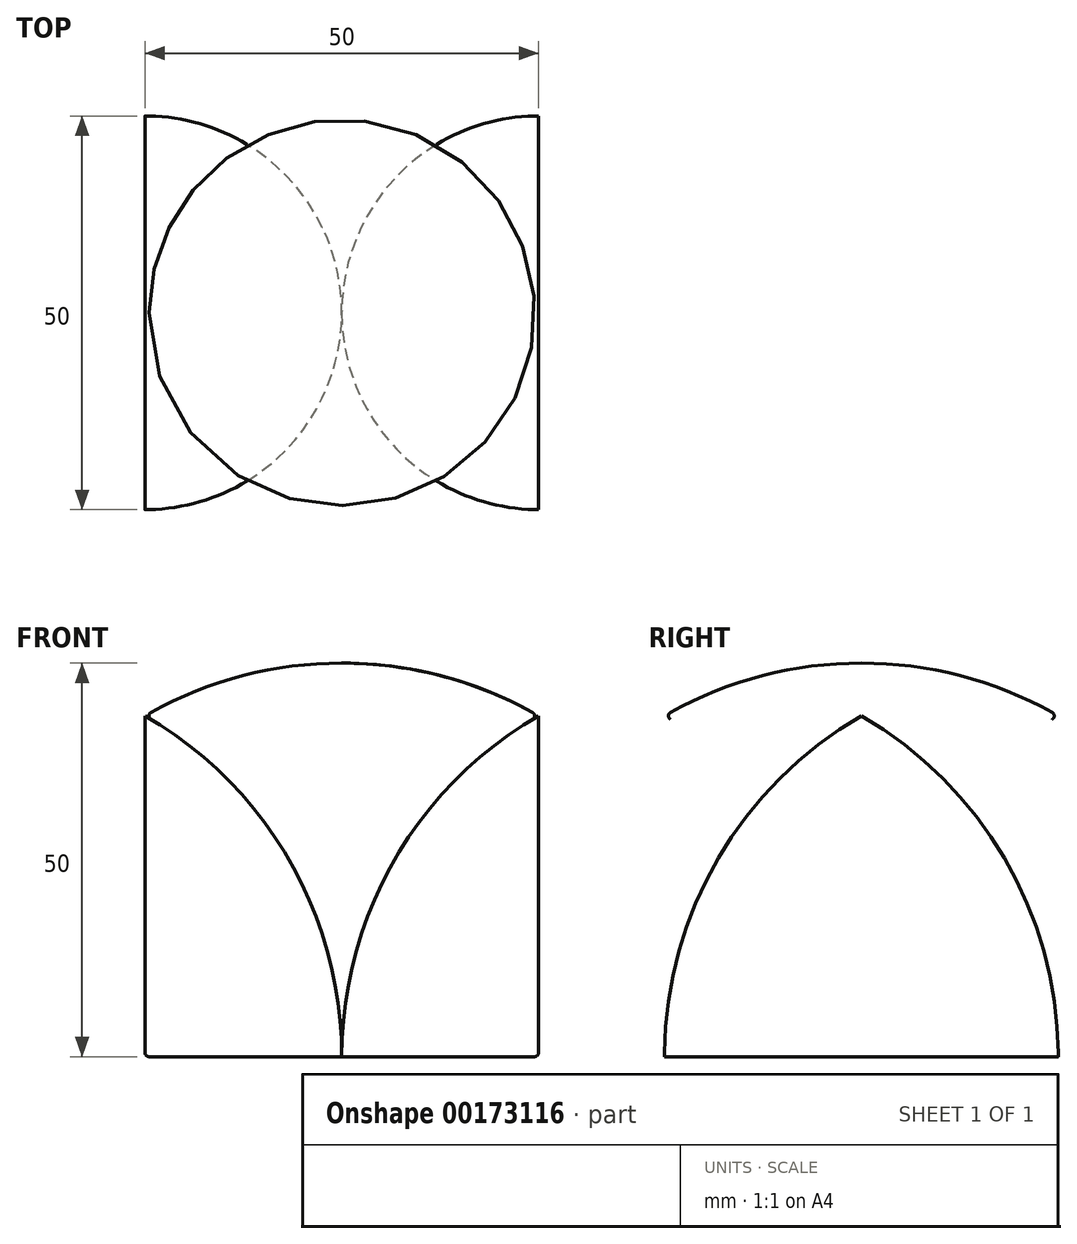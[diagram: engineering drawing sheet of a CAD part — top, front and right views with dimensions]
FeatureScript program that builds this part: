
annotation { "Feature Type Name" : "Feature", "Feature Type Description" : "" }
export const myFeature = defineFeature(function(context is Context, id is Id, definition is map)
    precondition{}
    {
        {
            var Q0;
            Q0=qCreatedBy(makeId("Front.planeOp"),FACE);
            var sketch = newSketch(context, id + "F0", { "sketchPlane" : qUnion([Q0])});
            skArc(sketch, "E0", {"start": v(-25, 43.3) * mm, "mid": v(0, -50) * mm, "end": v(25, 43.3) * mm});
            skCircle(sketch, "E1", {"center": v(-50, 0) * mm, "radius": 50 * mm});
            skCircle(sketch, "E2", {"center": v(50, 0) * mm, "radius": 50 * mm});
            skLineSegment(sketch, "E3", {"start": v(0, 50) * mm, "end": v(0, 0) * mm});
            skLineSegment(sketch, "E4", {"start": v(25, 43.3) * mm, "end": v(25, 0) * mm});
            skLineSegment(sketch, "E5", {"start": v(25, 0) * mm, "end": v(25, -43.3) * mm});
            skLineSegment(sketch, "E6", {"start": v(-25, 43.3) * mm, "end": v(-25, -43.3) * mm});
            skLineSegment(sketch, "E7", {"start": v(25, 0) * mm, "end": v(-25, 0) * mm});
            skCircle(sketch, "E8", {"center": v(0, 0) * mm, "radius": 50 * mm});
            skSolve(sketch);
        }
        {
            var Q0;
            {var subQ0=sQuery(id+"F0.wireOp",EDGE,"E3");Q0=makeQuery(id+"F0.imprint","IMPRINT",FACE,{"disambiguationData":[TD([[makeQuery(id+"F0.imprint","IMPRINT",EDGE,{"derivedFrom":subQ0}),1.0]])]});}
            var Q1;
            Q1=sQuery(id+"F0.wireOp",EDGE,"E3");
            revolve(context, id + "F1", {"entities" : qUnion([Q0]), "axis" : qUnion([Q1]), "revolveType" : RevolveType.FULL});
        }
        {
            var Q0;
            {var subQ3=sQuery(id+"F0.wireOp",EDGE,"E4");Q0=makeQuery(id+"F0.imprint","IMPRINT",FACE,{"disambiguationData":[TD([[makeQuery(id+"F0.imprint","IMPRINT",EDGE,{"derivedFrom":subQ3}),1.0]])]});}
            var Q1;
            {var subQ3=sQuery(id+"F0.wireOp",EDGE,"E5");Q1=makeQuery(id+"F0.imprint","IMPRINT",FACE,{"disambiguationData":[TD([[makeQuery(id+"F0.imprint","IMPRINT",EDGE,{"derivedFrom":subQ3}),1.0]])]});}
            var Q2;
            Q2=sQuery(id+"F0.wireOp",EDGE,"E4");
            revolve(context, id + "F2", {"entities" : qUnion([Q0, Q1]), "axis" : qUnion([Q2]), "revolveType" : RevolveType.FULL});
        }
        {
            var Q0;
            {var subQ0=sQuery(id+"F0.wireOp",EDGE,"E4");Q0=makeQuery(id+"F0.imprint","IMPRINT",FACE,{"disambiguationData":[TD([[makeQuery(id+"F0.imprint","IMPRINT",EDGE,{"derivedFrom":subQ0}),-1.0]])]});}
            extrude(context, id + "F3", {"entities" : qUnion([Q0]), "operationType" : NewBodyOperationType.REMOVE, "depth" : 60 * mm, "symmetric" : true});
        }
        {
            var Q0;
            {var subQ0=sQuery(id+"F0.wireOp",EDGE,"E6");var subQ5=makeQuery(id+"F0.imprint","INTERSECT",VERTEX,{"derivedFrom":[subQ0,sQuery(id+"F0.wireOp",EDGE,"E7")]});Q0=makeQuery(id+"F0.imprint","IMPRINT",FACE,{"disambiguationData":[TD([[makeQuery(id+"F0.imprint","IMPRINT",EDGE,{"disambiguationData":[TD([[subQ5,1.0]])],"derivedFrom":subQ0}),-1.0]])]});}
            var Q1;
            Q1=sQuery(id+"F0.wireOp",EDGE,"E6");
            revolve(context, id + "F4", {"entities" : qUnion([Q0]), "axis" : qUnion([Q1]), "revolveType" : RevolveType.FULL});
        }
        {
            var Q0;
            {var subQ0=sQuery(id+"F0.wireOp",EDGE,"E6");var subQ3=sQuery(id+"F0.wireOp",EDGE,"E7");var subQ5=makeQuery(id+"F0.imprint","INTERSECT",VERTEX,{"derivedFrom":[subQ0,subQ3]});Q0=makeQuery(id+"F0.imprint","IMPRINT",FACE,{"disambiguationData":[TD([[makeQuery(id+"F0.imprint","IMPRINT",EDGE,{"disambiguationData":[TD([[subQ5,1.0]])],"derivedFrom":subQ0}),1.0]])]});}
            extrude(context, id + "F5", {"entities" : qUnion([Q0]), "operationType" : NewBodyOperationType.REMOVE, "oppositeDirection" : true, "depth" : 60 * mm, "symmetric" : true});
        }
        {
            var Q0;
            {var subQ0=sQuery(id+"F0.wireOp",EDGE,"E3");Q0=makeQuery(id+"F0.imprint","IMPRINT",FACE,{"disambiguationData":[TD([[makeQuery(id+"F0.imprint","IMPRINT",EDGE,{"derivedFrom":subQ0}),-1.0]])]});}
            var Q1;
            Q1=sQuery(id+"F0.wireOp",EDGE,"E3");
            revolve(context, id + "F6", {"entities" : qUnion([Q0]), "axis" : qUnion([Q1]), "revolveType" : RevolveType.FULL});
        }
        {
            var Q0;
            Q0=makeQuery(id+"F1.opRevolve","SWEPT_BODY",BODY,{"disambiguationData":[OSD([sQuery(id+"F0.wireOp",EDGE,"E2"),sQuery(id+"F0.wireOp",EDGE,"E3"),sQuery(id+"F0.wireOp",EDGE,"E8")])]});
            deleteBodies(context, id + "F7", {"entities" : qUnion([Q0])});
        }
        {
            var Q0;
            Q0=makeQuery(id+"F5.boolean.opBoolean","INTERSECT",EDGE,{"disambiguationData":[OD(0.0)],"derivedFrom":[makeQuery(id+"F4.opRevolve","SWEPT_FACE",FACE,{"disambiguationData":[OSD([sQuery(id+"F0.wireOp",EDGE,"E8")])]}),makeQuery(id+"F5.opExtrude","SWEPT_FACE",FACE,{"disambiguationData":[OSD([sQuery(id+"F0.wireOp",EDGE,"E6")])]})]});
            var Q1;
            Q1=makeQuery(id+"F5.boolean.opBoolean","INTERSECT",EDGE,{"derivedFrom":[makeQuery(id+"F4.opRevolve","SWEPT_FACE",FACE,{"disambiguationData":[OSD([sQuery(id+"F0.wireOp",EDGE,"E8")])]}),makeQuery(id+"F5.opExtrude","SWEPT_FACE",FACE,{"disambiguationData":[OSD([sQuery(id+"F0.wireOp",EDGE,"E7")])]})]});
            var Q2;
            Q2=makeQuery(id+"F3.boolean.opBoolean","INTERSECT",EDGE,{"derivedFrom":[makeQuery(id+"F2.opRevolve","SWEPT_FACE",FACE,{"disambiguationData":[OSD([sQuery(id+"F0.wireOp",EDGE,"E8")])]}),makeQuery(id+"F3.opExtrude","SWEPT_FACE",FACE,{"disambiguationData":[OSD([sQuery(id+"F0.wireOp",EDGE,"E7")])]})]});
            var Q3;
            Q3=makeQuery(id+"F3.boolean.opBoolean","INTERSECT",EDGE,{"disambiguationData":[OD(0.0)],"derivedFrom":[makeQuery(id+"F2.opRevolve","SWEPT_FACE",FACE,{"disambiguationData":[OSD([sQuery(id+"F0.wireOp",EDGE,"E8")])]}),makeQuery(id+"F3.opExtrude","SWEPT_FACE",FACE,{"disambiguationData":[OSD([sQuery(id+"F0.wireOp",EDGE,"E4")])]})]});
            var Q4;
            Q4=makeQuery(id+"F6.opRevolve","SWEPT_EDGE",EDGE,{"disambiguationData":[OSD([sQuery(id+"F0.wireOp",EDGE,"E1"),sQuery(id+"F0.wireOp",EDGE,"E6"),sQuery(id+"F0.wireOp",EDGE,"E8")])]});
            fillet(context, id + "F8", {"entities" : qUnion([Q0, Q1, Q2, Q3, Q4]), "radius" : 0.5 * mm, "tangentPropagation" : true, "allowEdgeOverflow" : false});
        }
        {
            var Q0;
            Q0=makeQuery(id+"F3.boolean.opBoolean","COPY",EDGE,{"derivedFrom":makeQuery(id+"F3.opExtrude","SWEPT_EDGE",EDGE,{"disambiguationData":[OSD([sQuery(id+"F0.wireOp",EDGE,"E4"),sQuery(id+"F0.wireOp",EDGE,"E5"),sQuery(id+"F0.wireOp",EDGE,"E7")])]})});
            var Q1;
            Q1=makeQuery(id+"F5.boolean.opBoolean","COPY",EDGE,{"derivedFrom":makeQuery(id+"F5.opExtrude","SWEPT_EDGE",EDGE,{"disambiguationData":[OSD([sQuery(id+"F0.wireOp",EDGE,"E6"),sQuery(id+"F0.wireOp",EDGE,"E7")])]})});
            fillet(context, id + "F9", {"entities" : qUnion([Q0, Q1]), "radius" : 0.5 * mm, "tangentPropagation" : true, "allowEdgeOverflow" : false});
        }
    });
